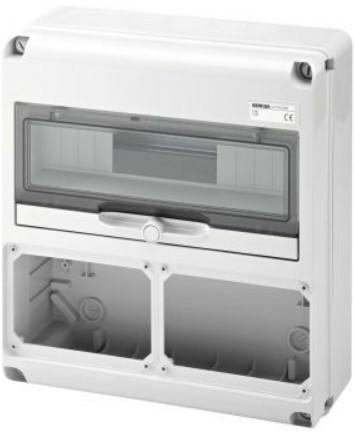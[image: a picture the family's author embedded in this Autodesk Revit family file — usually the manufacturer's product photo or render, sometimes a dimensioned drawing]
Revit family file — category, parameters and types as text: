
# Revit family: Building-IEC309Boards-GEWISS-68QDIN-DISTRIBUTION-BOARD-14MOD_2SOCKET-OUTLETS_IB_ORIZ
name_source: partatom
category: Apparecchi elettrici
units: mm (PartAtom-declared; Revit-internal decimal feet)

## family parameters
Condiviso = No
Host = Superficie
Mantenere orientamento annotazione = Sì
Punto di calcolo locali = Sì
Quota connettore circolare = Usa diametro
Taglio con vuoti quando caricato = No
Tipo di parte = Normale

## types (1)
- GW68006N - Q-DIN 14M.2 FLANGES S.O.BL.HOR.SBF IP65
    Accordance with Standards = EN 60208 - EN 60670-1 - IEC 60670-24
    Catalogue = BUILDING
    Catalogue Range = 68 QDIN
    Colour = Grey RAL 7035
    Descrizione = Q-DIN 14M.2 FLANGES S.O.BL.HOR.SBF IP65
    Dispersible power A (W) = 24
    Dispersible power B (W) = 64
    EAN code = 8011564744776
    Electrocod = 2242
    Glow Wire Test = 650°C
    Houseable interloc. socket. = 2 IB Horiz. 16/32A SBF IP44 side by side
    Houseable socket = 2 IB Horiz. 16/32A SBF IP44 side by side
    IDF = f4e0af6f-28e3-4579-84bf-f9a4547446fa
    IDT = 025e6d85-348f-4064-8737-2dc7c756130e
    IP degree = IP65
    Immagine tipo = GW68006N.jpg
    Installation type = Surface-mounting
    Insulation class = II
    Modello = GW68006N
    No. IB socket-outlets houseable = 2 IB Horiz. 16/32A SBF IP44 side by side
    No. of blank lids supplied = 1 IB 16/32A
    No. of modules EN 50022 = 14
    No. of provided blank lids = 1 IB 16/32A
    Operating temperature: = -25 +40 °C
    POMELLO = bianco
    PRESA = rosso
    Produttore = GEWISS S.p.A.
    Prospetto di default = 1219 mm
    SEO = Board
    STRUTTURA = RAL - 7035
    STRUTTURA ALTA = Poche
    Shock resistance = IK08
    Spostamento_S = 1000 mm  [stored 3.28084 ft]
    Technical sheet = https://www.gewiss.com
    Thermo-pressure with ball = 70
    URL = https://www.gewiss.com
    VETRO = Vetro
    Version file RFA = 21.5
    Version type = Empty
    Working temperature = -25 ÷ +40 °C

note: source unit labels omitted for Thermo-pressure with ball — the stored unit's dimension contradicts the parameter name (converter mislabeling)

note: [stored X ft] marks values corroborated as IEEE doubles in the binary element streams (Revit-internal decimal feet)

## geometry (parser evidence)
native form markers: Sweep x3
no freeform markers — native parametric forms only
